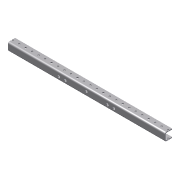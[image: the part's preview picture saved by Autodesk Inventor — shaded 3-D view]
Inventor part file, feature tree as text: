
AUTODESK INVENTOR PART (.ipt)
format: ipt  version: 2013 (Build 170138000, 138)  size: 211,968 bytes
history: native  units: in
note: dims shown in document units (in); Inventor stores cm internally (conversion verified against a paired STEP export)
features: projected_geometry x8, extrude x2, sketch x2, other x1, imported_body x1
ambient origin geometry x8: Origin, YZ Plane, XZ Plane, XY Plane, X Axis, Y Axis, Z Axis, Center Point
feature tree (14):
  other  "Short C Channel for drive1"
  extrude  "Extrusion1"  TaperAngle=0.0deg  [1 undecoded]
  extrude  "Extrusion2"  [1 undecoded]
  imported_body  "Base1"
  sketch  "Sketch1"  dims[d1=0.0in d3=0.0in]
  projected_geometry  "Projected Loop1"
  projected_geometry  "Projected Loop2"
  projected_geometry  "Projected Loop3"
  projected_geometry  "Projected Loop4"
  sketch  "Sketch2"
  projected_geometry  "Projected Loop5"
  projected_geometry  "Projected Loop6"
  projected_geometry  "Projected Loop7"
  projected_geometry  "Projected Loop8"
note: 2 required parameter values undecoded (feature->parameter linkage not recoverable at this tier; creation-order binding heuristic only, values carry confidence <= 0.55)
